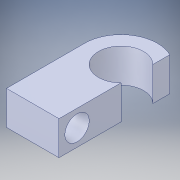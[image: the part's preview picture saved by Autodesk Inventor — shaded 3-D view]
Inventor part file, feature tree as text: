
AUTODESK INVENTOR PART (.ipt)
format: ipt  version: 2018 (Build 220112000, 112)  size: 112,640 bytes
history: native  units: in
note: dims shown in document units (in); Inventor stores cm internally (conversion verified against a paired STEP export)
features: extrude x1, sketch x1, other x1
ambient origin geometry x8: Origin, YZ Plane, XZ Plane, XY Plane, X Axis, Y Axis, Z Axis, Center Point
bodies: Solid1 (feature_tree)
feature tree (3):
  extrude  "Extrusion1"  TaperAngle=0.0deg  [1 undecoded]
  sketch  "Sketch1"  dims[d0=0.2697in d1=0.0in d2=0.0in]
  other  "Cut-Extrude1"
note: 1 required parameter value undecoded (feature->parameter linkage not recoverable at this tier; creation-order binding heuristic only, values carry confidence <= 0.55)
